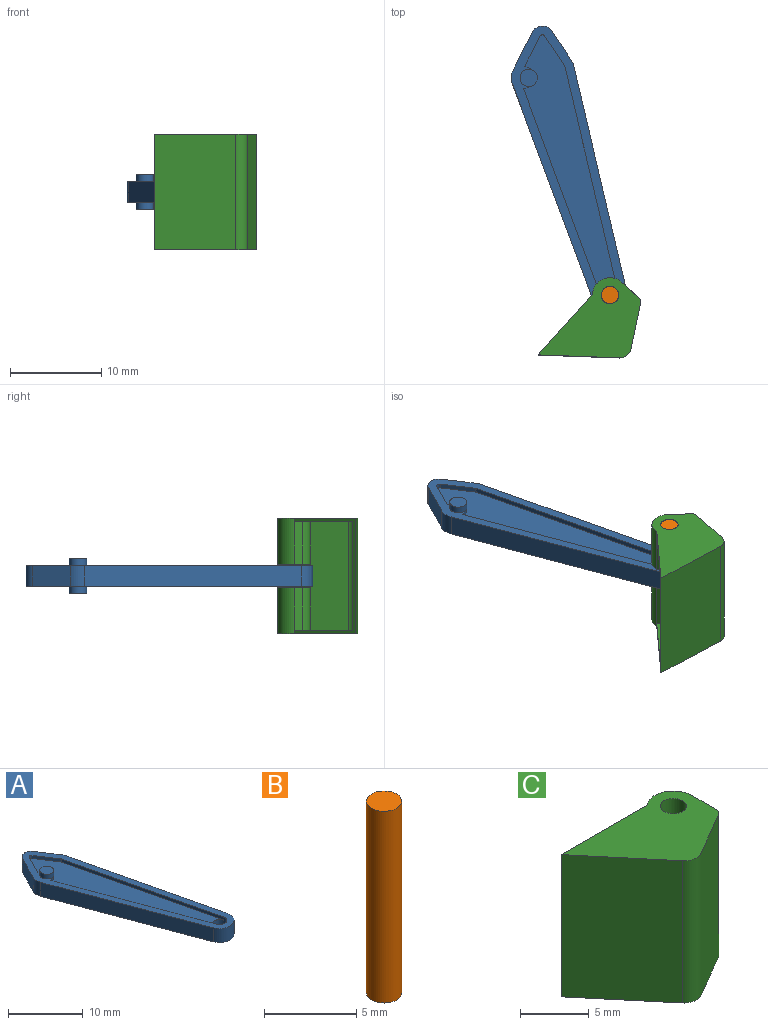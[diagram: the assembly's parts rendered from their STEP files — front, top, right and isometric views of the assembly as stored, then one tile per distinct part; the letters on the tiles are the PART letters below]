
ASSEMBLY  parts=3 mates=2
PART A: 35 faces, bbox 12.7x31.4x3.8 mm
  f0: cylinder r=0.95mm len=2.29mm, axis (0,0,-1), area 10.5mm2, adj f1,f10,f16,f23,f24,f26,f33,f34
  f1: plane 31.38x12.7mm, normal (0,0,1), area 64mm2, adj f0,f2,f3,f4,f5,f6,f7,f8
  f2: plane 4.13x2.29mm, normal (-0.89,0.45,0), area 10.6mm2, adj f1,f3,f9,f10
  f3: cylinder r=1.91mm len=2.29mm, axis (0,0,-1), area 3.6mm2, adj f1,f2,f4,f10
  f4: plane 23.79x8.89mm, normal (-0.94,-0.35,0), area 58.1mm2, adj f1,f3,f5,f10
  f5: cylinder r=1.91mm len=3.69mm, axis (0,0,-1), area 13.1mm2, adj f1,f4,f6,f10
  f6: plane 24.78x5.85mm, normal (0.97,0.23,0), area 58.2mm2, adj f1,f5,f7,f10
  f7: cylinder r=1.27mm len=2.29mm, axis (0,0,-1), area 1mm2, adj f1,f6,f8,f10
  f8: plane 3.28x2.29mm, normal (0.84,0.55,0), area 9mm2, adj f1,f7,f9,f10
  f9: cylinder r=1.27mm len=2.29mm, axis (0,0,-1), area 6.1mm2, adj f1,f2,f8,f10
  f10: plane 31.38x12.7mm, normal (0,0,-1), area 64mm2, adj f0,f2,f3,f4,f5,f6,f7,f8
  f11: plane 1.91x1.91mm, normal (0,0,-1), area 2.9mm2, adj f12
  f12: cylinder r=0.95mm len=1.91mm, axis (0,0,-1), area 5.6mm2, adj f10,f11,f25,f27,f28,f34
  f13: cylinder r=0.95mm len=1.91mm, axis (0,0,-1), area 5.6mm2, adj f1,f14,f15,f21,f22,f24
  f14: plane 1.91x1.91mm, normal (0,0,1), area 2.9mm2, adj f13
  f15: plane 0.26x0.1mm, normal (0,0,-1), area 0mm2, adj f13,f22
  f16: plane 24.78x5.85mm, normal (-0.97,-0.23,0), area 12.9mm2, adj f0,f1,f17,f24
  f17: cylinder r=0.32mm len=0.51mm, axis (0,0,1), area 0.1mm2, adj f1,f16,f18,f24
  f18: plane 3.28x2.15mm, normal (-0.84,-0.55,0), area 2mm2, adj f1,f17,f19,f24
  f19: cylinder r=0.32mm len=0.55mm, axis (0,0,1), area 0.3mm2, adj f1,f18,f20,f24
  f20: plane 3.27x1.65mm, normal (0.89,-0.45,0), area 1.9mm2, adj f1,f19,f21,f24
  f21: plane 0.85x0.51mm, normal (0.45,0.89,0), area 0.5mm2, adj f1,f13,f20,f24
  f22: plane 1.02x0.51mm, normal (0.35,-0.94,0), area 0.6mm2, adj f1,f13,f15,f23,f24
  f23: plane 22.91x8.56mm, normal (0.94,0.35,0), area 12.4mm2, adj f0,f1,f22,f24
  f24: plane 28.85x10.38mm, normal (0,0,1), area 96.2mm2, adj f0,f13,f16,f17,f18,f19,f20,f21
  f25: plane 0.26x0.1mm, normal (0,0,1), area 0mm2, adj f12,f27
  f26: plane 22.91x8.56mm, normal (0.94,0.35,0), area 12.4mm2, adj f0,f10,f27,f34
  f27: plane 1.02x0.51mm, normal (0.35,-0.94,0), area 0.6mm2, adj f10,f12,f25,f26,f34
  f28: plane 0.85x0.51mm, normal (0.45,0.89,0), area 0.5mm2, adj f10,f12,f29,f34
  f29: plane 3.27x1.65mm, normal (0.89,-0.45,0), area 1.9mm2, adj f10,f28,f30,f34
  f30: cylinder r=0.32mm len=0.55mm, axis (0,0,-1), area 0.3mm2, adj f10,f29,f31,f34
  f31: plane 3.28x2.15mm, normal (-0.84,-0.55,0), area 2mm2, adj f10,f30,f32,f34
  f32: cylinder r=0.32mm len=0.51mm, axis (0,0,-1), area 0.1mm2, adj f10,f31,f33,f34
  f33: plane 24.78x5.85mm, normal (-0.97,-0.23,0), area 12.9mm2, adj f0,f10,f32,f34
  f34: plane 28.85x10.38mm, normal (0,0,-1), area 96.2mm2, adj f0,f12,f26,f27,f28,f29,f30,f31
PART B: 3 faces, bbox 1.9x1.9x12.7 mm
  f0: cylinder r=0.95mm len=12.7mm, axis (0,0,-1), area 76mm2, adj f1,f2
  f1: plane 1.91x1.91mm, normal (0,0,1), area 2.9mm2, adj f0
  f2: plane 1.91x1.91mm, normal (0,0,-1), area 2.9mm2, adj f0
PART C: 26 faces, bbox 12x7.7x12.7 mm
  f0: plane 12.7x2.54mm, normal (1,0,0), area 27.4mm2, adj f1,f9,f10,f13,f14,f23,f24,f25
  f1: cylinder r=1.91mm len=5.08mm, axis (0,0,-1), area 22mm2, adj f0,f5,f11,f14,f24
  f2: cylinder r=0.95mm len=5.08mm, axis (0,0,-1), area 30.4mm2, adj f14,f24
  f3: plane 11.94x2.35mm, normal (-0.53,-0.85,0), area 30.6mm2, adj f4,f15,f16,f20,f21,f22,f24,f25
  f4: cylinder r=1.65mm len=4.7mm, axis (0,0,1), area 10.6mm2, adj f3,f5,f20,f24
  f5: plane 4.7x0.88mm, normal (-0.94,0.34,0), area 4.4mm2, adj f1,f4,f20,f24
  f6: plane 12.7x6.81mm, normal (-0.77,-0.64,0), area 112.9mm2, adj f7,f11,f13,f14
  f7: cylinder r=1.27mm len=12.7mm, axis (0,0,-1), area 22.6mm2, adj f6,f8,f13,f14
  f8: plane 12.7x4.39mm, normal (0.5,-0.86,0), area 64.5mm2, adj f7,f9,f13,f14
  f9: cylinder r=0.64mm len=12.7mm, axis (0,0,-1), area 8.4mm2, adj f0,f8,f13,f14
  f10: cylinder r=1.91mm len=5.08mm, axis (0,0,-1), area 22mm2, adj f0,f11,f13,f17,f25
  f11: plane 12.7x8.89mm, normal (0,1,0), area 10.7mm2, adj f1,f6,f10,f13,f14,f18,f20,f21
  f12: cylinder r=0.95mm len=5.08mm, axis (0,0,-1), area 30.4mm2, adj f13,f25
  f13: plane 12.03x7.72mm, normal (0,0,1), area 55.5mm2, adj f0,f6,f7,f8,f9,f10,f11,f12
  f14: plane 12.03x7.72mm, normal (0,0,-1), area 55.5mm2, adj f0,f1,f2,f6,f7,f8,f9,f11
  f15: plane 11.94x4.4mm, normal (-0.5,0.86,0), area 60.8mm2, adj f3,f19,f20,f21
  f16: cylinder r=1.65mm len=4.7mm, axis (0,0,1), area 10.6mm2, adj f3,f17,f21,f25
  f17: plane 4.7x0.88mm, normal (-0.94,0.34,0), area 4.4mm2, adj f10,f16,f21,f25
  f18: plane 11.94x6.65mm, normal (0.77,0.64,0), area 103.6mm2, adj f11,f19,f20,f21
  f19: cylinder r=1.02mm len=11.94mm, axis (0,0,1), area 17mm2, adj f15,f18,f20,f21
  f20: plane 11.27x7.01mm, normal (0,0,1), area 42mm2, adj f3,f4,f5,f11,f15,f18,f19
  f21: plane 11.27x7.01mm, normal (0,0,-1), area 42mm2, adj f3,f11,f15,f16,f17,f18,f19
  f22: cylinder r=1.91mm len=2.54mm, axis (0,0,1), area 0.2mm2, adj f3,f23,f24,f25
  f23: plane 2.54x1.91mm, normal (0,1,0), area 4.8mm2, adj f0,f22,f24,f25
  f24: plane 3.81x3.56mm, normal (0,0,1), area 8.4mm2, adj f0,f1,f2,f3,f4,f5,f22,f23
  f25: plane 3.81x3.56mm, normal (0,0,-1), area 8.4mm2, adj f0,f3,f10,f12,f16,f17,f22,f23
PLACE A t=(-3.08,14.46,-18.57)mm fixed
PLACE B t=(43.88,4.89,-18.57)mm
PLACE C rot(axis=(0,0,1),48deg) t=(43.88,4.89,-18.57)mm
MATE revolute B.f0 <-> A.f0  axis (0,0,-1) through (43.88,4.89,-18.57)mm
MATE revolute C.f2 <-> B.f0  axis (0,0,-1) through (43.88,4.89,-19.84)mm
